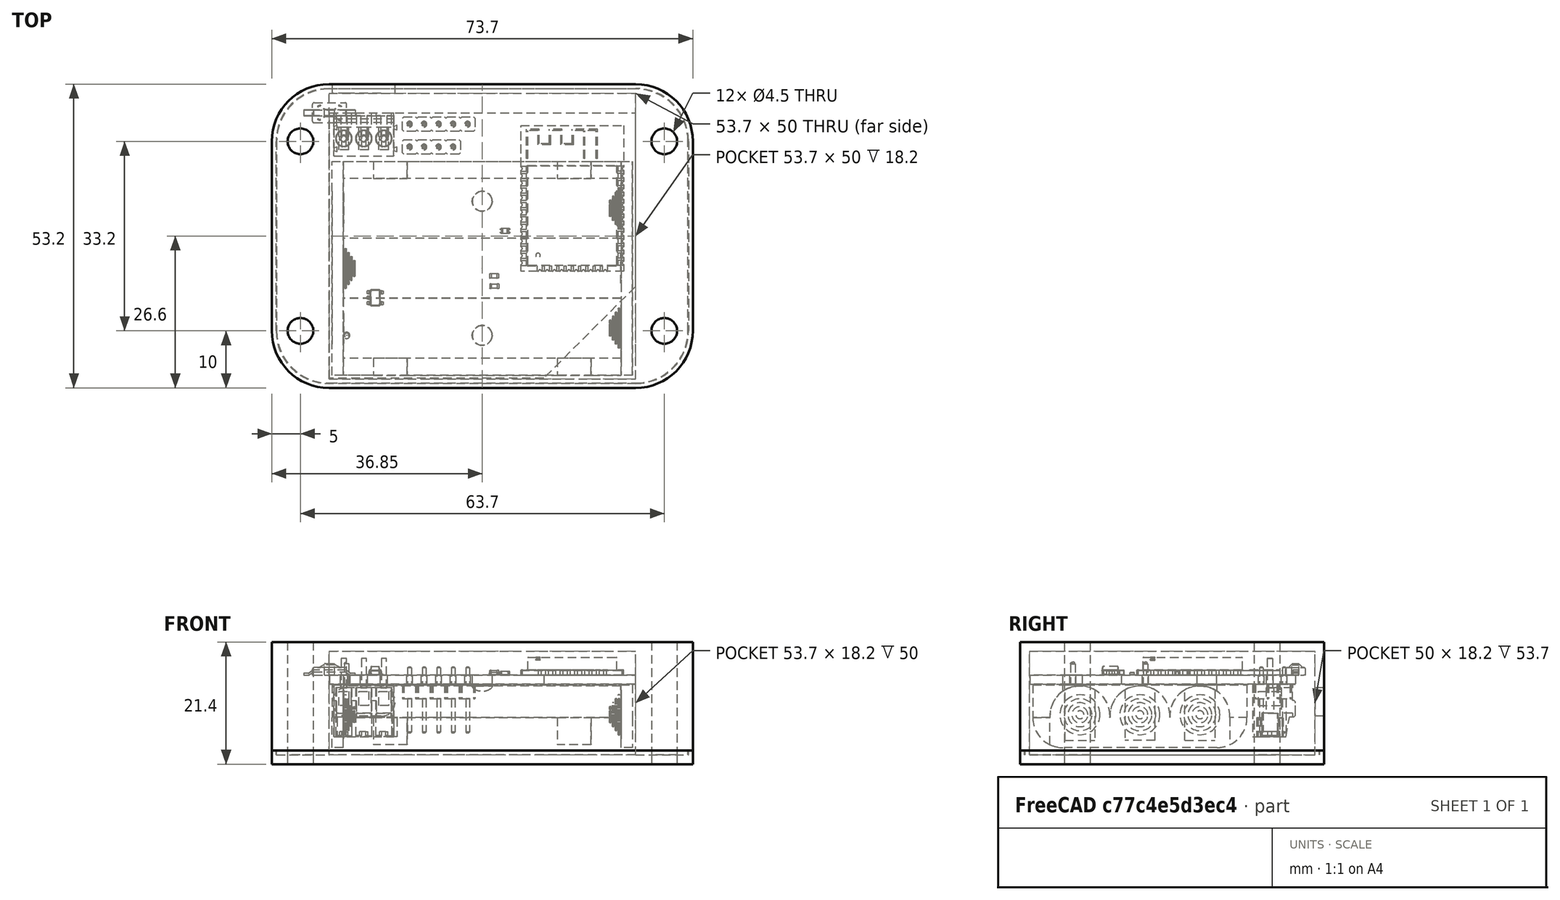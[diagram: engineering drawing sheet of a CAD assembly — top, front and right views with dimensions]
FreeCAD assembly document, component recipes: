
FREECAD ASSEMBLY — COMPONENT RECIPES ("mail-to-telegram")

This assembly document has 4 components, labeled P0..P3 below (a component is one placed body or linked part). 3 of them carry a construction recipe — the FreeCAD feature program that regenerates the part from scratch, quoted from this document or its linked companion documents; the rest are supplied as boundary geometry only. No exploded tour is included for this assembly.
COMPONENT P0 — geometry summary ("mail-to-telegram"; no construction recipe available for this part):
  bounding box: 53.5 x 46.5 x 15.8 mm
  tessellated surface: 61,528 triangles
  volume: 11700 mm^3 (30% of its bounding box)
COMPONENT P1 — recipe-attached ("Body", modeled in this document).
Construction recipe (the document's own serialized feature program — sketch geometry with constraints, then the solid features built on it; lengths are millimeters unless a unit is written):

FEATURE [PartDesign::FeatureBase] BaseFeature
  BaseFeature = -> Fillet
FEATURE [PartDesign::Plane] DatumPlane
  Length = 104.707
  MapMode = 5
  Placement = pos=(0,0,5.8) rot=(0,0,1;0rad)
  ResizeMode = 0
  Support = -> [BaseFeature]
  Width = 89.3065
FEATURE [Sketcher::SketchObject] Sketch
  ExternalGeometry = -> [BaseFeature]
  FullyConstrained = true
  MapMode = 5
  Placement = pos=(0,0,5.8) rot=(0,0,1;0rad)
  Support = -> [BaseFeature]
  sketch-geometry (6):
    g0: Circle CenterX=-5.1 CenterY=-5 CenterZ=0 NormalX=0 NormalY=0 NormalZ=1 AngleXU=0 Radius=2
    g1: LineSegment StartX=-10.1 StartY=-21.6 StartZ=0 EndX=0 EndY=-21.6 EndZ=0
    g2: Circle CenterX=-5.1 CenterY=-38.2 CenterZ=0 NormalX=0 NormalY=0 NormalZ=1 AngleXU=0 Radius=2
    g3: LineSegment StartX=26.75 StartY=5 StartZ=0 EndX=26.75 EndY=0 EndZ=0
    g4: Circle CenterX=58.6 CenterY=-5 CenterZ=0 NormalX=0 NormalY=0 NormalZ=1 AngleXU=0 Radius=2
    g5: Circle CenterX=58.6 CenterY=-38.2 CenterZ=0 NormalX=0 NormalY=0 NormalZ=1 AngleXU=0 Radius=2
  constraints (14):
    c: Symmetric(g-3,g-3,g0)
    c: Diameter(g0) = 4
    c: Horizontal(g1)
    c: Symmetric(g-4,g-4,g1)
    c: PointOnObject(g1,g-2)
    c: Diameter(g2) = 4
    c: Symmetric(g2,g0,g1)
    c: PointOnObject(g3,g-1)
    c: Vertical(g3)
    c: Symmetric(g-5,g-5,g3)
    c: Diameter(g4) = 4
    c: Diameter(g5) = 4
    c: Symmetric(g4,g0,g3)
    c: Symmetric(g5,g2,g3)
FEATURE [PartDesign::Hole] Hole
  BaseFeature = -> BaseFeature
  Depth = 25
  DepthType = 1
  Diameter = 4.5
  DrillForDepth = false
  DrillPoint = 1
  DrillPointAngle = 118
  HoleCutCountersinkAngle = 90
  HoleCutCustomValues = false
  HoleCutDepth = 0
  HoleCutDiameter = 6.1
  HoleCutType = 0
  ModelActualThread = false
  Profile = -> Sketch
  Tapered = false
  TaperedAngle = 90
  ThreadAngle = 60
  ThreadClass = 0
  ThreadCutOffInner = 0.0757772
  ThreadCutOffOuter = 0.151554
  ThreadDirection = 0
  ThreadFit = 0
  ThreadPitch = 0.7
  ThreadSize = 11
  ThreadType = 1
  Threaded = false
FEATURE [PartDesign::Plane] DatumPlane001
  AttachmentOffset = pos=(0,0,-1.6) rot=(0,0,1;0rad)
  Length = 104.707
  MapMode = 5
  Placement = pos=(0,0,-14) rot=(1,0,0;3.14159rad)
  ResizeMode = 0
  Support = -> [Hole]
  Width = 89.3065
FEATURE [PartDesign::Body] Body
  BaseFeature = -> Fillet
  Group = -> [BaseFeature,DatumPlane,Sketch,Hole,DatumPlane001]
  Origin = -> Origin009
  Tip = -> Hole
COMPONENT P2 — recipe-attached ("Enclosure", modeled in this document).
Construction recipe (the document's own serialized feature program — sketch geometry with constraints, then the solid features built on it; lengths are millimeters unless a unit is written):

FEATURE [PartDesign::FeatureBase] BaseFeature001
  BaseFeature = -> Slice_child0
FEATURE [PartDesign::Plane] DatumPlane003
  Length = 104.707
  MapMode = 5
  Placement = pos=(0,0,-14) rot=(1,0,0;3.14159rad)
  ResizeMode = 0
  Support = -> [BaseFeature001]
  Width = 89.3065
FEATURE [Sketcher::SketchObject] Sketch002
  ExternalGeometry = -> [BaseFeature001]
  FullyConstrained = true
  MapMode = 5
  Placement = pos=(0,0,-14) rot=(1,0,0;3.14159rad)
  Support = -> [BaseFeature001]
  sketch-geometry (16):
    g0: LineSegment StartX=-0.1 StartY=48.2 StartZ=0 EndX=53.6 EndY=48.2 EndZ=0
    g1: LineSegment StartX=63.6 StartY=38.2 StartZ=0 EndX=63.6 EndY=5 EndZ=0
    g2: LineSegment StartX=53.6 StartY=-5 StartZ=0 EndX=-0.1 EndY=-5 EndZ=0
    g3: LineSegment StartX=-10.1 StartY=5 StartZ=0 EndX=-10.1 EndY=38.2 EndZ=0
    g4: ArcOfCircle CenterX=-0.1 CenterY=38.2 CenterZ=0 NormalX=0 NormalY=0 NormalZ=1 AngleXU=0 Radius=10 StartAngle=1.5708 EndAngle=3.14159
    g5: ArcOfCircle CenterX=-0.1 CenterY=5 CenterZ=0 NormalX=0 NormalY=0 NormalZ=1 AngleXU=0 Radius=10 StartAngle=3.14159 EndAngle=4.71239
    g6: ArcOfCircle CenterX=53.6 CenterY=5 CenterZ=0 NormalX=0 NormalY=0 NormalZ=1 AngleXU=0 Radius=10 StartAngle=4.71239 EndAngle=6.28319
    g7: ArcOfCircle CenterX=53.6 CenterY=38.2 CenterZ=0 NormalX=0 NormalY=0 NormalZ=1 AngleXU=0 Radius=10 StartAngle=0 EndAngle=1.5708
    g8: LineSegment StartX=-0.1 StartY=47.35 StartZ=0 EndX=53.6 EndY=47.35 EndZ=0
    g9: LineSegment StartX=62.75 StartY=38.2 StartZ=0 EndX=62.75 EndY=5 EndZ=0
    g10: LineSegment StartX=53.6 StartY=-4.15 StartZ=0 EndX=-0.1 EndY=-4.15 EndZ=0
    g11: LineSegment StartX=-9.25 StartY=5 StartZ=0 EndX=-9.25 EndY=38.2 EndZ=0
    g12: ArcOfCircle CenterX=-0.1 CenterY=38.2 CenterZ=0 NormalX=0 NormalY=0 NormalZ=1 AngleXU=0 Radius=9.15 StartAngle=1.5708 EndAngle=3.14159
    g13: ArcOfCircle CenterX=-0.1 CenterY=5 CenterZ=0 NormalX=0 NormalY=0 NormalZ=1 AngleXU=0 Radius=9.15 StartAngle=3.14159 EndAngle=4.71239
    g14: ArcOfCircle CenterX=53.6 CenterY=5 CenterZ=0 NormalX=0 NormalY=0 NormalZ=1 AngleXU=0 Radius=9.15 StartAngle=4.71239 EndAngle=6.28319
    g15: ArcOfCircle CenterX=53.6 CenterY=38.2 CenterZ=0 NormalX=0 NormalY=0 NormalZ=1 AngleXU=0 Radius=9.15 StartAngle=0 EndAngle=1.5708
  constraints (36):
    c: Horizontal(g0)
    c: Horizontal(g2)
    c: Vertical(g1)
    c: Vertical(g3)
    c: Tangent(g0,g4) = 1.5708
    c: Tangent(g3,g4) = 1.5708
    c: Tangent(g2,g5) = 1.5708
    c: Tangent(g3,g5) = 1.5708
    c: Tangent(g2,g6) = 1.5708
    c: Tangent(g1,g6) = 1.5708
    c: Tangent(g0,g7) = 1.5708
    c: Tangent(g1,g7) = 1.5708
    c: Equal(g6,g5)
    c: Equal(g5,g4)
    c: Equal(g4,g7)
    c: Coincident(g-3,g4)
    c: Coincident(g-4,g6)
    c: Equal(g-3,g4)
    c: Horizontal(g8)
    c: Horizontal(g10)
    c: Vertical(g9)
    c: Vertical(g11)
    c: Tangent(g8,g12) = 1.5708
    c: Tangent(g11,g12) = 1.5708
    c: Tangent(g10,g13) = 1.5708
    c: Tangent(g11,g13) = 1.5708
    c: Tangent(g10,g14) = 1.5708
    c: Tangent(g9,g14) = 1.5708
    c: Tangent(g8,g15) = 1.5708
    c: Tangent(g9,g15) = 1.5708
    c: Equal(g14,g13)
    c: Equal(g13,g12)
    c: Equal(g12,g15)
    c: Coincident(g12,g4)
    c: Coincident(g14,g6)
    c: DistanceY(g8,g0) = 0.85
FEATURE [PartDesign::Pocket] Pocket
  BaseFeature = -> BaseFeature001
  Length = 0.8
  Length2 = 100
  Profile = -> Sketch002
  Type = 0
FEATURE [Sketcher::SketchObject] Sketch003
  FullyConstrained = true
  MapMode = 5
  Placement = pos=(0,5,0) rot=(0,0.707107,0.707107;3.14159rad)
  Support = -> [Pocket]
  sketch-geometry (5):
    g0: ArcOfCircle CenterX=-9 CenterY=-4.7 CenterZ=0 NormalX=0 NormalY=0 NormalZ=1 AngleXU=0 Radius=2.5 StartAngle=1.5708 EndAngle=4.71239
    g1: ArcOfCircle CenterX=-3 CenterY=-4.7 CenterZ=0 NormalX=0 NormalY=0 NormalZ=1 AngleXU=0 Radius=2.5 StartAngle=4.71239 EndAngle=7.85398
    g2: LineSegment StartX=-9 StartY=-7.2 StartZ=0 EndX=-3 EndY=-7.2 EndZ=0
    g3: LineSegment StartX=-9 StartY=-2.2 StartZ=0 EndX=-3 EndY=-2.2 EndZ=0
    g4: GeomPoint X=-6 Y=-2.2 Z=0
  constraints (11):
    c: Tangent(g0,g3) = 1.5708
    c: Tangent(g0,g2) = -1.5708
    c: Tangent(g2,g1) = -1.5708
    c: Tangent(g3,g1) = 1.5708
    c: Horizontal(g2)
    c: Equal(g0,g1)
    c: DistanceY(g1,g1) = 5
    c: DistanceX(g0,g1) = 6
    c: DistanceY(g1,g-1) = 2.2
    c: Symmetric(g1,g0,g4)
    c: DistanceX(g4,g-1) = 6
FEATURE [PartDesign::Pocket] Pocket001
  BaseFeature = -> Pocket
  Length = 5
  Length2 = 100
  Profile = -> Sketch003
  Type = 2
FEATURE [PartDesign::Body] Body001  label="Enclosure"
  BaseFeature = -> Slice_child0
  Group = -> [BaseFeature001,DatumPlane003,Sketch002,Pocket,Sketch003,Pocket001]
  Origin = -> Origin010
  Tip = -> Pocket001
COMPONENT P3 — recipe-attached ("Lid", modeled in this document).
Construction recipe (the document's own serialized feature program — sketch geometry with constraints, then the solid features built on it; lengths are millimeters unless a unit is written):

FEATURE [PartDesign::FeatureBase] BaseFeature002
  BaseFeature = -> Slice_child1
FEATURE [PartDesign::Plane] DatumPlane002
  Length = 104.707
  MapMode = 5
  Placement = pos=(0,0,-14) rot=(0,0,1;0rad)
  ResizeMode = 0
  Support = -> [BaseFeature002]
  Width = 89.3065
FEATURE [Sketcher::SketchObject] Sketch001
  ExternalGeometry = -> [BaseFeature002]
  FullyConstrained = true
  MapMode = 5
  Placement = pos=(0,0,-14) rot=(0,0,1;0rad)
  Support = -> [DatumPlane002]
  sketch-geometry (16):
    g0: LineSegment StartX=-0.1 StartY=5 StartZ=0 EndX=53.6 EndY=5 EndZ=0
    g1: LineSegment StartX=63.6 StartY=-5 StartZ=0 EndX=63.6 EndY=-38.2 EndZ=0
    g2: LineSegment StartX=53.6 StartY=-48.2 StartZ=0 EndX=-0.1 EndY=-48.2 EndZ=0
    g3: LineSegment StartX=-10.1 StartY=-38.2 StartZ=0 EndX=-10.1 EndY=-5 EndZ=0
    g4: ArcOfCircle CenterX=-0.1 CenterY=-5 CenterZ=0 NormalX=0 NormalY=0 NormalZ=1 AngleXU=0 Radius=10 StartAngle=1.5708 EndAngle=3.14159
    g5: ArcOfCircle CenterX=53.6 CenterY=-5 CenterZ=0 NormalX=0 NormalY=0 NormalZ=1 AngleXU=0 Radius=10 StartAngle=0 EndAngle=1.5708
    g6: ArcOfCircle CenterX=53.6 CenterY=-38.2 CenterZ=0 NormalX=0 NormalY=0 NormalZ=1 AngleXU=0 Radius=10 StartAngle=4.71239 EndAngle=6.28319
    g7: ArcOfCircle CenterX=-0.1 CenterY=-38.2 CenterZ=0 NormalX=0 NormalY=0 NormalZ=1 AngleXU=0 Radius=10 StartAngle=3.14159 EndAngle=4.71239
    g8: LineSegment StartX=-0.1 StartY=4.25 StartZ=0 EndX=53.6 EndY=4.25 EndZ=0
    g9: LineSegment StartX=62.85 StartY=-5 StartZ=0 EndX=62.85 EndY=-38.2 EndZ=0
    g10: LineSegment StartX=53.6 StartY=-47.45 StartZ=0 EndX=-0.1 EndY=-47.45 EndZ=0
    g11: LineSegment StartX=-9.35 StartY=-38.2 StartZ=0 EndX=-9.35 EndY=-5 EndZ=0
    g12: ArcOfCircle CenterX=-0.1 CenterY=-5 CenterZ=0 NormalX=0 NormalY=0 NormalZ=1 AngleXU=0 Radius=9.25 StartAngle=1.5708 EndAngle=3.14159
    g13: ArcOfCircle CenterX=53.6 CenterY=-5 CenterZ=0 NormalX=0 NormalY=0 NormalZ=1 AngleXU=0 Radius=9.25 StartAngle=0 EndAngle=1.5708
    g14: ArcOfCircle CenterX=53.6 CenterY=-38.2 CenterZ=0 NormalX=0 NormalY=0 NormalZ=1 AngleXU=0 Radius=9.25 StartAngle=4.71239 EndAngle=6.28319
    g15: ArcOfCircle CenterX=-0.1 CenterY=-38.2 CenterZ=0 NormalX=0 NormalY=0 NormalZ=1 AngleXU=0 Radius=9.25 StartAngle=3.14159 EndAngle=4.71239
  constraints (36):
    c: Horizontal(g0)
    c: Horizontal(g2)
    c: Vertical(g1)
    c: Vertical(g3)
    c: Tangent(g3,g4) = 1.5708
    c: Tangent(g0,g4) = 1.5708
    c: Tangent(g0,g5) = 1.5708
    c: Tangent(g1,g5) = 1.5708
    c: Tangent(g2,g6) = 1.5708
    c: Tangent(g1,g6) = 1.5708
    c: Tangent(g3,g7) = 1.5708
    c: Tangent(g2,g7) = 1.5708
    c: Equal(g4,g-3)
    c: Equal(g-3,g7)
    c: Equal(g7,g6)
    c: Equal(g6,g5)
    c: Coincident(g4,g-3)
    c: Coincident(g-4,g6)
    c: Horizontal(g8)
    c: Horizontal(g10)
    c: Vertical(g9)
    c: Vertical(g11)
    c: Tangent(g11,g12) = 1.5708
    c: Tangent(g8,g12) = 1.5708
    c: Tangent(g8,g13) = 1.5708
    c: Tangent(g9,g13) = 1.5708
    c: Tangent(g10,g14) = 1.5708
    c: Tangent(g9,g14) = 1.5708
    c: Tangent(g11,g15) = 1.5708
    c: Tangent(g10,g15) = 1.5708
    c: Equal(g15,g14)
    c: Equal(g14,g13)
    c: Equal(g12,g13)
    c: Coincident(g4,g12)
    c: Coincident(g14,g6)
    c: DistanceY(g8,g0) = 0.75
FEATURE [PartDesign::Pad] Pad
  BaseFeature = -> BaseFeature002
  Direction = (1,1,1)
  Length = 0.8
  Length2 = 100
  Profile = -> Sketch001
  Type = 0
FEATURE [PartDesign::Body] Body002  label="Lid"
  BaseFeature = -> Slice_child1
  Group = -> [BaseFeature002,DatumPlane002,Sketch001,Pad]
  Origin = -> Origin011
  Tip = -> Pad
PROVENANCE & LICENSES
A FreeCAD (.FCStd) document from a public repository crawl; recipes are the document's own serialized feature recipes (and, for linked parts, companion documents' recipes).
License: as declared in the source repository (recorded in the dataset sidecar).
